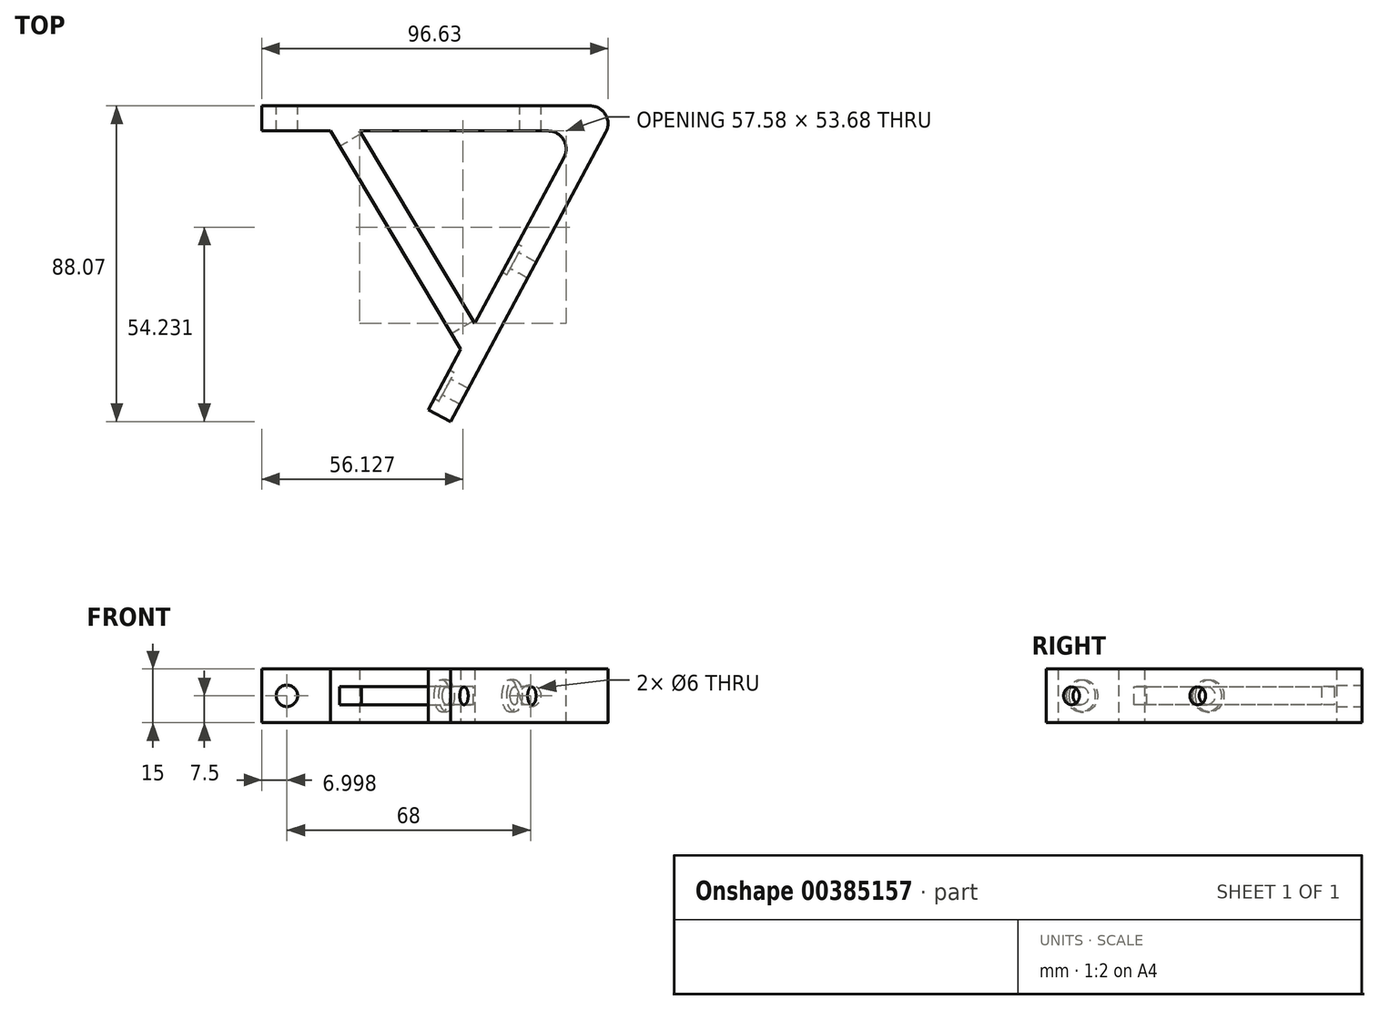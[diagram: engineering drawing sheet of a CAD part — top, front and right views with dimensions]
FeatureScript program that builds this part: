
annotation { "Feature Type Name" : "Feature", "Feature Type Description" : "" }
export const myFeature = defineFeature(function(context is Context, id is Id, definition is map)
    precondition{}
    {
        {
            var Q0;
            Q0=qCreatedBy(makeId("Top.planeOp"),FACE);
            var sketch = newSketch(context, id + "F0", { "sketchPlane" : qUnion([Q0])});
            skLineSegment(sketch, "E0", {"start": v(-52.63, 0) * mm, "end": v(47.37, 0) * mm});
            skLineSegment(sketch, "E1", {"start": v(47.37, 0) * mm, "end": v(0, -88.07) * mm});
            skLineSegment(sketch, "E2", {"start": v(-33.45, -7) * mm, "end": v(2.92, -67.86) * mm});
            skLineSegment(sketch, "E3.0", {"start": v(-52.63, -7) * mm, "end": v(-33.45, -7) * mm});
            skLineSegment(sketch, "E4", {"start": v(-52.63, 0) * mm, "end": v(-52.63, -7) * mm});
            skLineSegment(sketch, "E5", {"start": v(0, -88.07) * mm, "end": v(-6.16, -84.75) * mm});
            skPoint(sketch, "E6.orphan", {"position": v(-37.63, 0) * mm});
            skLineSegment(sketch, "E7.trimOffspring", {"start": v(-25.3, -7) * mm, "end": v(6.78, -60.68) * mm});
            skLineSegment(sketch, "E8.trimOffspring", {"start": v(-25.3, -7) * mm, "end": v(35.66, -7) * mm});
            skLineSegment(sketch, "E9.trimOffspring", {"start": v(35.66, -7) * mm, "end": v(6.78, -60.68) * mm});
            skPoint(sketch, "E10.orphan", {"position": v(7.1, -74.86) * mm});
            skLineSegment(sketch, "E11.trimOffspring", {"start": v(2.92, -67.86) * mm, "end": v(-6.16, -84.75) * mm});
            skSolve(sketch);
        }
        {
            var Q0;
            Q0=makeQuery(id+"F0.imprint","IMPRINT",FACE,{"disambiguationData":[TD([[makeQuery(id+"F0.imprint","IMPRINT",EDGE,{"derivedFrom":sQuery(id+"F0.wireOp",EDGE,"E0")}),-1.0]])]});
            extrude(context, id + "F1", {"entities" : qUnion([Q0]), "depth" : 15 * mm});
        }
        {
            var Q0;
            Q0=makeQuery(id+"F1.opExtrude","SWEPT_FACE",FACE,{"disambiguationData":[OSD([sQuery(id+"F0.wireOp",EDGE,"E9.trimOffspring")])]});
            var sketch = newSketch(context, id + "F2", { "sketchPlane" : qUnion([Q0])});
            skPoint(sketch, "E12", {"position": v(29.56, 7.5) * mm});
            skPoint(sketch, "E13", {"position": v(69.56, 7.5) * mm});
            skSolve(sketch);
        }
        {
            var Q0;
            Q0=sQuery(id+"F2.wireOp",VERTEX,"E13");
            var Q1;
            Q1=sQuery(id+"F2.wireOp",VERTEX,"E12");
            var Q2;
            Q2=makeQuery(id+"F1.opExtrude","SWEPT_BODY",BODY,{"disambiguationData":[OSD([sQuery(id+"F0.wireOp",EDGE,"E0"),sQuery(id+"F0.wireOp",EDGE,"E1"),sQuery(id+"F0.wireOp",EDGE,"E2"),sQuery(id+"F0.wireOp",EDGE,"E3.0"),sQuery(id+"F0.wireOp",EDGE,"E4"),sQuery(id+"F0.wireOp",EDGE,"E5"),sQuery(id+"F0.wireOp",EDGE,"E7.trimOffspring"),sQuery(id+"F0.wireOp",EDGE,"E8.trimOffspring"),sQuery(id+"F0.wireOp",EDGE,"E9.trimOffspring"),sQuery(id+"F0.wireOp",EDGE,"E11.trimOffspring")])]});
            hole(context, id + "F3", {"style" : HoleStyle.C_BORE, "endStyle" : HoleEndStyle.THROUGH, "holeDiameter" : 5 * mm, "cBoreDiameter" : 9 * mm, "cBoreDepth" : 1.5 * mm, "isTappedThrough" : true, "tappedDepth" : 12 * mm, "tapClearance" : 3, "locations" : qUnion([Q0, Q1]), "scope" : qUnion([Q2])});
        }
        {
            var Q0;
            Q0=makeQuery(id+"F1.opExtrude","SWEPT_FACE",FACE,{"disambiguationData":[OSD([sQuery(id+"F0.wireOp",EDGE,"E2")])]});
            var sketch = newSketch(context, id + "F4", { "sketchPlane" : qUnion([Q0])});
            skLineSegment(sketch, "E14.0.0", {"start": v(-11.15, 0) * mm, "end": v(59.75, 0) * mm});
            skLineSegment(sketch, "E14.0.1", {"start": v(59.75, 0) * mm, "end": v(59.75, 15) * mm});
            skLineSegment(sketch, "E14.0.2", {"start": v(59.75, 15) * mm, "end": v(-11.15, 15) * mm});
            skLineSegment(sketch, "E14.0.3", {"start": v(-11.15, 15) * mm, "end": v(-11.15, 0) * mm});
            skLineSegment(sketch, "E15.0", {"start": v(-6.15, 10) * mm, "end": v(-6.15, 5) * mm});
            skLineSegment(sketch, "E15.1", {"start": v(54.75, 10) * mm, "end": v(-6.15, 10) * mm});
            skLineSegment(sketch, "E15.2", {"start": v(54.75, 5) * mm, "end": v(54.75, 10) * mm});
            skLineSegment(sketch, "E15.3", {"start": v(-6.15, 5) * mm, "end": v(54.75, 5) * mm});
            skSolve(sketch);
        }
        {
            var Q0;
            Q0=makeQuery(id+"F4.imprint","IMPRINT",FACE,{"disambiguationData":[TD([[makeQuery(id+"F4.imprint","IMPRINT",EDGE,{"derivedFrom":sQuery(id+"F4.wireOp",EDGE,"E15.0")}),1.0]])]});
            extrude(context, id + "F5", {"entities" : qUnion([Q0]), "operationType" : NewBodyOperationType.REMOVE, "endBound" : BoundingType.UP_TO_NEXT, "oppositeDirection" : true, "depth" : 25 * mm});
        }
        {
            var Q0;
            Q0=makeQuery(id+"F1.opExtrude","SWEPT_FACE",FACE,{"disambiguationData":[OSD([sQuery(id+"F0.wireOp",EDGE,"E0")])]});
            var sketch = newSketch(context, id + "F6", { "sketchPlane" : qUnion([Q0])});
            skCircle(sketch, "E16", {"center": v(-22.37, 7.5) * mm, "radius": 3 * mm});
            skPoint(sketch, "E16.centerSnap0", {"position": v(-47.37, 7.5) * mm});
            skCircle(sketch, "E17", {"center": v(45.63, 7.5) * mm, "radius": 3 * mm});
            skPoint(sketch, "E17.centerSnap0", {"position": v(52.63, 7.5) * mm});
            skSolve(sketch);
        }
        {
            var Q0;
            Q0=makeQuery(id+"F6.imprint","IMPRINT",FACE,{"disambiguationData":[TD([[makeQuery(id+"F6.imprint","IMPRINT",EDGE,{"derivedFrom":sQuery(id+"F6.wireOp",EDGE,"E16")}),1.0]])]});
            var Q1;
            Q1=makeQuery(id+"F6.imprint","IMPRINT",FACE,{"disambiguationData":[TD([[makeQuery(id+"F6.imprint","IMPRINT",EDGE,{"derivedFrom":sQuery(id+"F6.wireOp",EDGE,"E17")}),1.0]])]});
            extrude(context, id + "F7", {"entities" : qUnion([Q0, Q1]), "operationType" : NewBodyOperationType.REMOVE, "endBound" : BoundingType.UP_TO_NEXT, "oppositeDirection" : true, "depth" : 25 * mm});
        }
        {
            var Q0;
            Q0=makeQuery(id+"F1.opExtrude","SWEPT_EDGE",EDGE,{"disambiguationData":[OSD([sQuery(id+"F0.wireOp",EDGE,"E8.trimOffspring"),sQuery(id+"F0.wireOp",EDGE,"E9.trimOffspring")])]});
            var Q1;
            Q1=makeQuery(id+"F1.opExtrude","SWEPT_EDGE",EDGE,{"disambiguationData":[OSD([sQuery(id+"F0.wireOp",EDGE,"E0"),sQuery(id+"F0.wireOp",EDGE,"E1")])]});
            fillet(context, id + "F8", {"entities" : qUnion([Q0, Q1]), "radius" : 5 * mm, "tangentPropagation" : true, "allowEdgeOverflow" : false});
        }
    });
